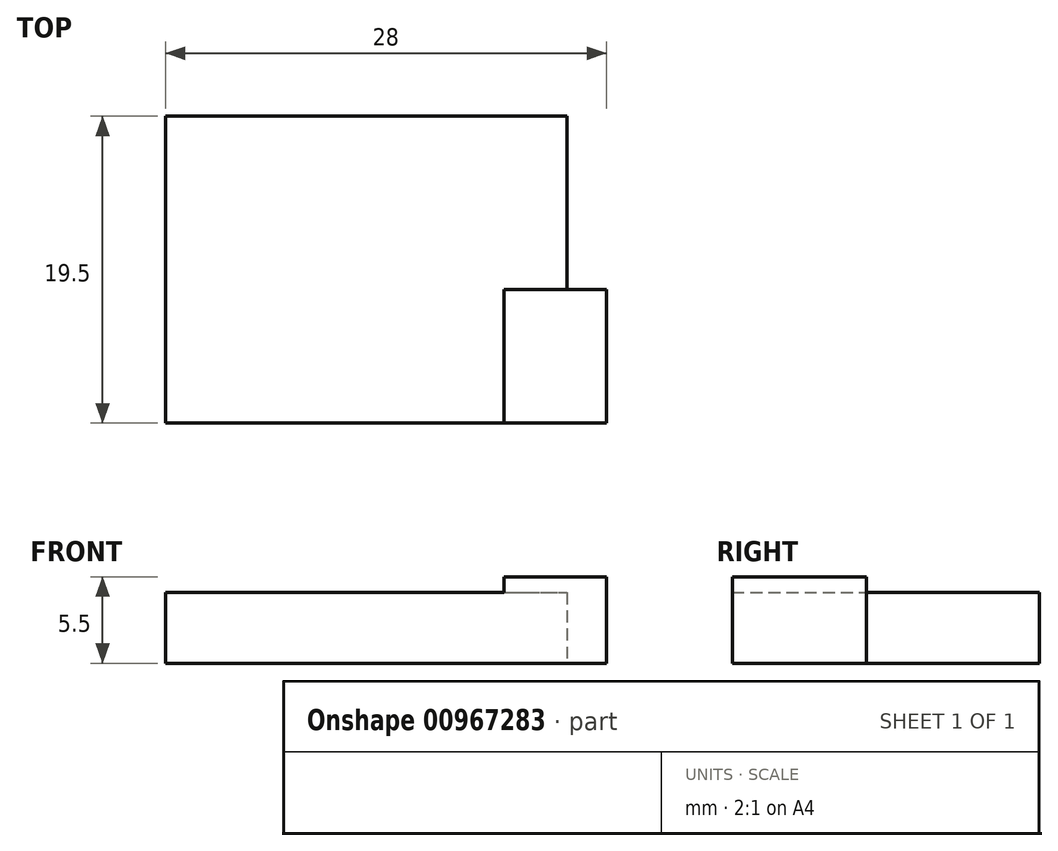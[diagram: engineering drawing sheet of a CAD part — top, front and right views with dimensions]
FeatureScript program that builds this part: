
annotation { "Feature Type Name" : "Feature", "Feature Type Description" : "" }
export const myFeature = defineFeature(function(context is Context, id is Id, definition is map)
    precondition{}
    {
        {
            var Q0;
            Q0=qCreatedBy(makeId("Top.planeOp"),FACE);
            var sketch = newSketch(context, id + "F0", { "sketchPlane" : qUnion([Q0])});
            skLineSegment(sketch, "E0.bottom", {"start": v(0, 19.5) * mm, "end": v(25.5, 19.5) * mm});
            skLineSegment(sketch, "E0.top", {"start": v(0, 0) * mm, "end": v(28, 0) * mm});
            skLineSegment(sketch, "E0.left", {"start": v(0, 19.5) * mm, "end": v(0, 0) * mm});
            skLineSegment(sketch, "E0.right", {"start": v(28, 8.5) * mm, "end": v(28, 0) * mm});
            skLineSegment(sketch, "E1", {"start": v(25.5, 19.5) * mm, "end": v(25.5, 8.5) * mm});
            skLineSegment(sketch, "E2", {"start": v(25.5, 8.5) * mm, "end": v(28, 8.5) * mm});
            skSolve(sketch);
        }
        {
            var Q0;
            Q0=makeQuery(id+"F0.imprint","IMPRINT",FACE,{"disambiguationData":[TD([[makeQuery(id+"F0.imprint","IMPRINT",EDGE,{"derivedFrom":sQuery(id+"F0.wireOp",EDGE,"E0.bottom")}),-1.0]])]});
            extrude(context, id + "F1", {"entities" : qUnion([Q0]), "depth" : 4.5 * mm});
        }
        {
            var Q0;
            Q0=makeQuery(id+"F1.opExtrude","CAP_FACE",FACE,{"disambiguationData":[OSD([sQuery(id+"F0.wireOp",EDGE,"E0.bottom"),sQuery(id+"F0.wireOp",EDGE,"E0.top"),sQuery(id+"F0.wireOp",EDGE,"E0.left"),sQuery(id+"F0.wireOp",EDGE,"E0.right"),sQuery(id+"F0.wireOp",EDGE,"E1"),sQuery(id+"F0.wireOp",EDGE,"E2")])],"isStart":false});
            var sketch = newSketch(context, id + "F2", { "sketchPlane" : qUnion([Q0])});
            skLineSegment(sketch, "E3.bottom", {"start": v(28, 0) * mm, "end": v(21.5, 0) * mm});
            skLineSegment(sketch, "E3.top", {"start": v(28, 8.5) * mm, "end": v(21.5, 8.5) * mm});
            skLineSegment(sketch, "E3.left", {"start": v(28, 0) * mm, "end": v(28, 8.5) * mm});
            skLineSegment(sketch, "E3.right", {"start": v(21.5, 0) * mm, "end": v(21.5, 8.5) * mm});
            skSolve(sketch);
        }
        {
            var Q0;
            Q0=qSketchRegion(id+"F2",true);
            extrude(context, id + "F3", {"entities" : qUnion([Q0]), "operationType" : NewBodyOperationType.ADD, "depth" : 1 * mm});
        }
    });
